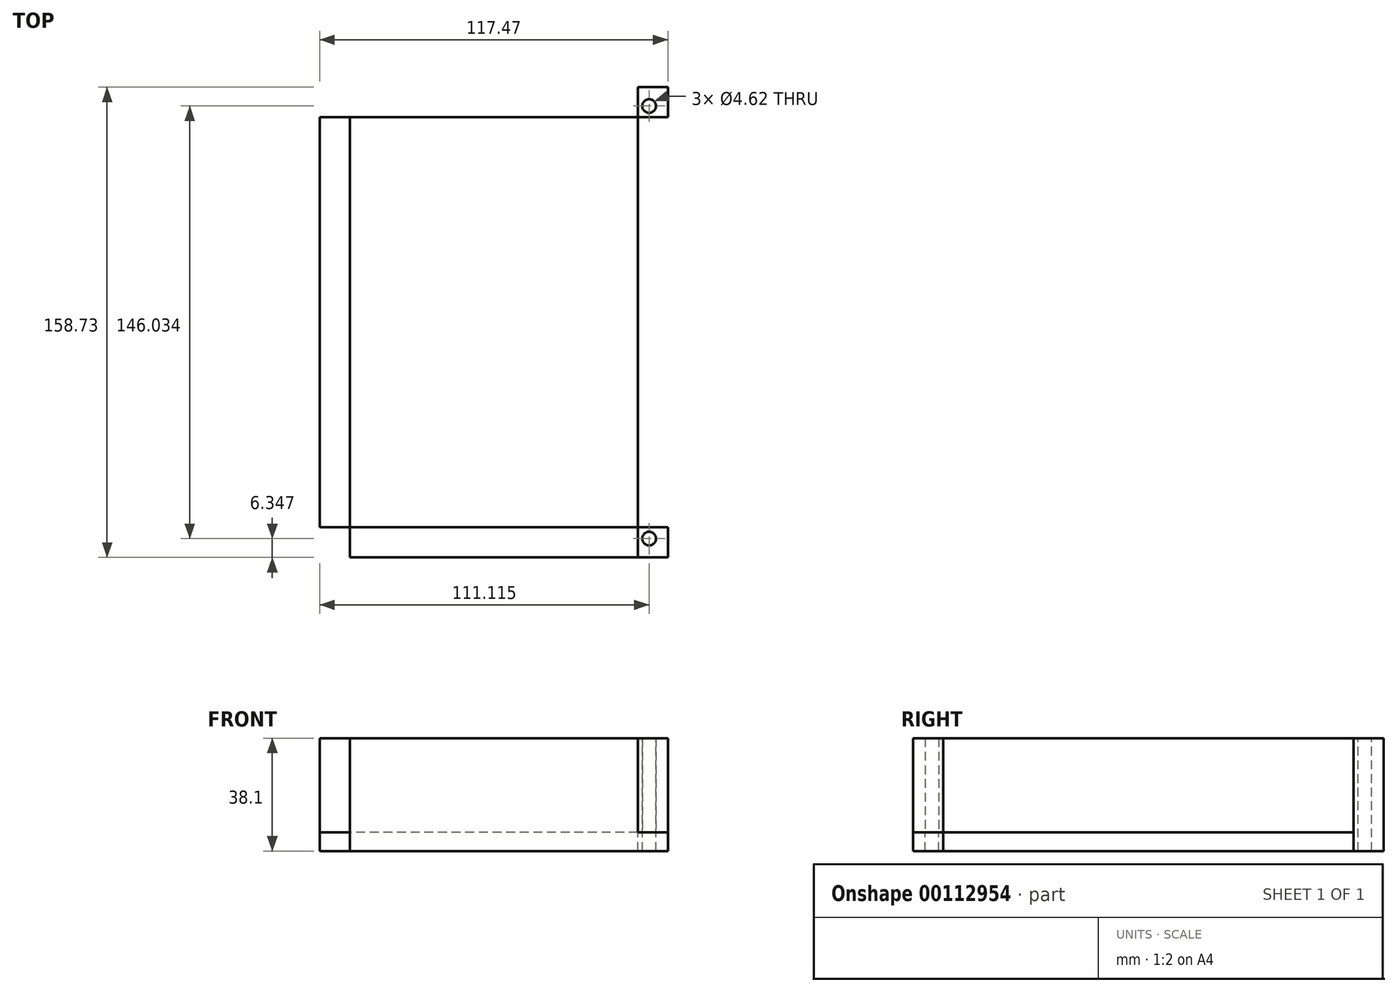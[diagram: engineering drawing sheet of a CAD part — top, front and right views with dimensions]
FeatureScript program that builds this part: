
annotation { "Feature Type Name" : "Feature", "Feature Type Description" : "" }
export const myFeature = defineFeature(function(context is Context, id is Id, definition is map)
    precondition{}
    {
        {
            var Q0;
            Q0=qCreatedBy(makeId("Top.planeOp"),FACE);
            var sketch = newSketch(context, id + "F0", { "sketchPlane" : qUnion([Q0])});
            skLineSegment(sketch, "E0", {"start": v(-95.22, 74.36) * mm, "end": v(-95.22, -84.37) * mm});
            skLineSegment(sketch, "E1", {"start": v(-95.22, 74.36) * mm, "end": v(22.25, 74.36) * mm});
            skLineSegment(sketch, "E2", {"start": v(22.25, 74.36) * mm, "end": v(22.25, -84.37) * mm});
            skLineSegment(sketch, "E3", {"start": v(22.25, -84.37) * mm, "end": v(-95.22, -84.37) * mm});
            skLineSegment(sketch, "E4", {"start": v(-95.22, 74.36) * mm, "end": v(-85.06, 74.36) * mm});
            skLineSegment(sketch, "E5", {"start": v(22.25, 74.36) * mm, "end": v(12.09, 74.36) * mm});
            skLineSegment(sketch, "E6", {"start": v(-95.22, 74.36) * mm, "end": v(-95.22, 61.66) * mm});
            skLineSegment(sketch, "E7", {"start": v(22.25, 74.36) * mm, "end": v(22.25, 64.2) * mm});
            skLineSegment(sketch, "E8", {"start": v(22.25, 64.2) * mm, "end": v(22.25, 74.36) * mm});
            skLineSegment(sketch, "E9", {"start": v(-95.22, -84.37) * mm, "end": v(-85.06, -84.37) * mm});
            skLineSegment(sketch, "E10.bottom", {"start": v(-95.22, -84.37) * mm, "end": v(-95.22, -84.37) * mm});
            skLineSegment(sketch, "E10.top", {"start": v(-95.22, -74.21) * mm, "end": v(-95.22, -74.21) * mm});
            skLineSegment(sketch, "E10.left", {"start": v(-95.22, -84.37) * mm, "end": v(-95.22, -74.21) * mm});
            skLineSegment(sketch, "E10.right", {"start": v(-95.22, -84.37) * mm, "end": v(-95.22, -74.21) * mm});
            skLineSegment(sketch, "E11.bottom", {"start": v(22.25, -84.37) * mm, "end": v(22.25, -84.37) * mm});
            skLineSegment(sketch, "E11.top", {"start": v(22.25, -74.21) * mm, "end": v(22.25, -74.21) * mm});
            skLineSegment(sketch, "E11.left", {"start": v(22.25, -84.37) * mm, "end": v(22.25, -74.21) * mm});
            skLineSegment(sketch, "E11.right", {"start": v(22.25, -84.37) * mm, "end": v(22.25, -74.21) * mm});
            skLineSegment(sketch, "E12.bottom", {"start": v(22.25, -84.37) * mm, "end": v(12.09, -84.37) * mm});
            skLineSegment(sketch, "E12.top", {"start": v(22.25, -84.37) * mm, "end": v(12.09, -84.37) * mm});
            skLineSegment(sketch, "E12.right", {"start": v(12.09, -84.37) * mm, "end": v(12.09, -84.37) * mm});
            skLineSegment(sketch, "E13", {"start": v(12.09, -84.37) * mm, "end": v(22.25, -84.37) * mm});
            skPoint(sketch, "E14.centerSnap0", {"position": v(-95.22, 68.01) * mm});
            skPoint(sketch, "E15.centerSnap0", {"position": v(22.25, 69.28) * mm});
            skPoint(sketch, "E16.centerSnap0", {"position": v(22.25, -79.3) * mm});
            skPoint(sketch, "E17.centerSnap1", {"position": v(-95.22, -79.3) * mm});
            skLineSegment(sketch, "E18", {"start": v(-85.06, -74.21) * mm, "end": v(-85.06, 61.66) * mm});
            skLineSegment(sketch, "E19", {"start": v(12.09, 61.66) * mm, "end": v(12.09, -74.21) * mm});
            skLineSegment(sketch, "E20", {"start": v(12.09, -74.21) * mm, "end": v(-85.06, -74.21) * mm});
            skLineSegment(sketch, "E21", {"start": v(-85.06, 74.36) * mm, "end": v(-85.06, 61.66) * mm});
            skLineSegment(sketch, "E22", {"start": v(12.09, 74.36) * mm, "end": v(12.09, 61.66) * mm});
            skLineSegment(sketch, "E23", {"start": v(12.09, -74.21) * mm, "end": v(22.25, -74.21) * mm});
            skLineSegment(sketch, "E24", {"start": v(12.09, -74.21) * mm, "end": v(12.09, -84.37) * mm});
            skLineSegment(sketch, "E25", {"start": v(-95.22, -74.21) * mm, "end": v(-85.06, -74.21) * mm});
            skLineSegment(sketch, "E26", {"start": v(-85.02, -87.14) * mm, "end": v(-85.06, -74.21) * mm});
            skLineSegment(sketch, "E27", {"start": v(-85.06, 61.66) * mm, "end": v(-85.06, 48.96) * mm});
            skLineSegment(sketch, "E28", {"start": v(-85.06, 48.96) * mm, "end": v(-85.06, 61.66) * mm});
            skLineSegment(sketch, "E29", {"start": v(12.09, 48.96) * mm, "end": v(12.09, 61.66) * mm});
            skLineSegment(sketch, "E30", {"start": v(-72.36, -74.21) * mm, "end": v(-85.06, -74.21) * mm});
            skLineSegment(sketch, "E31", {"start": v(-85.06, -74.21) * mm, "end": v(-85.06, -61.51) * mm});
            skLineSegment(sketch, "E32", {"start": v(-0.61, -74.21) * mm, "end": v(12.09, -74.21) * mm});
            skLineSegment(sketch, "E33", {"start": v(12.09, -61.51) * mm, "end": v(12.09, -74.21) * mm});
            skLineSegment(sketch, "E34", {"start": v(-95.22, -84.37) * mm, "end": v(-88.87, -84.37) * mm});
            skLineSegment(sketch, "E35", {"start": v(22.25, -84.37) * mm, "end": v(15.9, -84.37) * mm});
            skLineSegment(sketch, "E36", {"start": v(15.9, -84.37) * mm, "end": v(22.25, -84.37) * mm});
            skLineSegment(sketch, "E37", {"start": v(-95.22, 74.36) * mm, "end": v(-88.87, 74.36) * mm});
            skLineSegment(sketch, "E38", {"start": v(-88.87, 74.36) * mm, "end": v(-95.22, 74.36) * mm});
            skLineSegment(sketch, "E39", {"start": v(22.25, 74.36) * mm, "end": v(15.9, 74.36) * mm});
            skLineSegment(sketch, "E40", {"start": v(22.25, 64.2) * mm, "end": v(-95.22, 64.2) * mm});
            skLineSegment(sketch, "E41", {"start": v(22.25, 74.36) * mm, "end": v(22.25, 68.01) * mm});
            skCircle(sketch, "E42", {"center": v(15.9, 68.01) * mm, "radius": 2.31 * mm});
            skLineSegment(sketch, "E43", {"start": v(-95.22, 74.36) * mm, "end": v(-95.22, 68.01) * mm});
            skCircle(sketch, "E44", {"center": v(-88.87, 68.01) * mm, "radius": 2.31 * mm});
            skLineSegment(sketch, "E45", {"start": v(-95.22, -84.37) * mm, "end": v(-95.22, -78.02) * mm});
            skCircle(sketch, "E46", {"center": v(-88.87, -78.02) * mm, "radius": 2.31 * mm});
            skLineSegment(sketch, "E47", {"start": v(22.25, -84.37) * mm, "end": v(22.25, -78.02) * mm});
            skCircle(sketch, "E48", {"center": v(15.9, -78.02) * mm, "radius": 2.31 * mm});
            skSolve(sketch);
        }
        {
            var Q0;
            Q0=makeQuery(id+"F0.imprint","IMPRINT",FACE,{"disambiguationData":[TD([[makeQuery(id+"F0.imprint","IMPRINT",EDGE,{"derivedFrom":sQuery(id+"F0.wireOp",EDGE,"E32")}),1.0]])]});
            var Q1;
            Q1=makeQuery(id+"F0.imprint","IMPRINT",FACE,{"disambiguationData":[TD([[makeQuery(id+"F0.imprint","IMPRINT",EDGE,{"derivedFrom":sQuery(id+"F0.wireOp",EDGE,"cZfFtAw6-LTCG-etWa-Laot-MlDrLfI1tADb")}),1.0]])]});
            var Q2;
            Q2=makeQuery(id+"F0.imprint","IMPRINT",FACE,{"disambiguationData":[TD([[makeQuery(id+"F0.imprint","IMPRINT",EDGE,{"derivedFrom":sQuery(id+"F0.wireOp",EDGE,"E30")}),-1.0]])]});
            var Q3;
            Q3=makeQuery(id+"F0.imprint","IMPRINT",FACE,{"disambiguationData":[TD([[makeQuery(id+"F0.imprint","IMPRINT",EDGE,{"derivedFrom":sQuery(id+"F0.wireOp",EDGE,"E29")}),1.0]])]});
            var Q4;
            Q4=makeQuery(id+"F0.imprint","IMPRINT",FACE,{"disambiguationData":[TD([[makeQuery(id+"F0.imprint","IMPRINT",EDGE,{"derivedFrom":sQuery(id+"F0.wireOp",EDGE,"E11.right")}),1.0]])]});
            var Q5;
            Q5=makeQuery(id+"F0.imprint","IMPRINT",FACE,{"disambiguationData":[TD([[makeQuery(id+"F0.imprint","IMPRINT",EDGE,{"derivedFrom":sQuery(id+"F0.wireOp",EDGE,"E4")}),-1.0]])]});
            var Q6;
            {var subQ0=sQuery(id+"F0.wireOp",EDGE,"E9");Q6=makeQuery(id+"F0.imprint","IMPRINT",FACE,{"disambiguationData":[TD([[makeQuery(id+"F0.imprint","IMPRINT",EDGE,{"derivedFrom":subQ0}),1.0]])]});}
            var Q7;
            Q7=makeQuery(id+"F0.imprint","IMPRINT",FACE,{"disambiguationData":[TD([[makeQuery(id+"F0.imprint","IMPRINT",EDGE,{"derivedFrom":sQuery(id+"F0.wireOp",EDGE,"E18")}),-1.0]])]});
            var Q8;
            Q8=makeQuery(id+"F0.imprint","IMPRINT",FACE,{"disambiguationData":[TD([[makeQuery(id+"F0.imprint","IMPRINT",EDGE,{"derivedFrom":sQuery(id+"F0.wireOp",EDGE,"E2")}),-1.0]])]});
            var Q9;
            Q9=makeQuery(id+"F0.imprint","IMPRINT",FACE,{"disambiguationData":[TD([[makeQuery(id+"F0.imprint","IMPRINT",EDGE,{"derivedFrom":sQuery(id+"F0.wireOp",EDGE,"E20")}),1.0]])]});
            var Q10;
            Q10=makeQuery(id+"F0.imprint","IMPRINT",FACE,{"disambiguationData":[TD([[makeQuery(id+"F0.imprint","IMPRINT",EDGE,{"derivedFrom":sQuery(id+"F0.wireOp",EDGE,"E1")}),-1.0]])]});
            var Q11;
            Q11=makeQuery(id+"F0.imprint","IMPRINT",FACE,{"disambiguationData":[TD([[makeQuery(id+"F0.imprint","IMPRINT",EDGE,{"derivedFrom":sQuery(id+"F0.wireOp",EDGE,"E0")}),1.0]])]});
            var Q12;
            Q12=makeQuery(id+"F0.imprint","IMPRINT",FACE,{"disambiguationData":[TD([[makeQuery(id+"F0.imprint","IMPRINT",EDGE,{"derivedFrom":sQuery(id+"F0.wireOp",EDGE,"E5")}),1.0]])]});
            extrude(context, id + "F1", {"entities" : qUnion([Q0, Q1, Q2, Q3, Q4, Q5, Q6, Q7, Q8, Q9, Q10, Q11, Q12]), "oppositeDirection" : true, "depth" : 6.35 * mm});
        }
        {
            var Q0;
            Q0=makeQuery(id+"F0.imprint","IMPRINT",FACE,{"disambiguationData":[TD([[makeQuery(id+"F0.imprint","IMPRINT",EDGE,{"derivedFrom":sQuery(id+"F0.wireOp",EDGE,"E1")}),-1.0]])]});
            extrude(context, id + "F2", {"entities" : qUnion([Q0]), "operationType" : NewBodyOperationType.ADD, "depth" : 31.75 * mm});
        }
        {
            var Q0;
            Q0=makeQuery(id+"F0.imprint","IMPRINT",FACE,{"disambiguationData":[TD([[makeQuery(id+"F0.imprint","IMPRINT",EDGE,{"derivedFrom":sQuery(id+"F0.wireOp",EDGE,"E20")}),1.0]])]});
            extrude(context, id + "F3", {"entities" : qUnion([Q0]), "operationType" : NewBodyOperationType.ADD, "depth" : 31.75 * mm});
        }
        {
            var Q0;
            Q0=makeQuery(id+"F0.imprint","IMPRINT",FACE,{"disambiguationData":[TD([[makeQuery(id+"F0.imprint","IMPRINT",EDGE,{"derivedFrom":sQuery(id+"F0.wireOp",EDGE,"E2")}),-1.0]])]});
            extrude(context, id + "F4", {"entities" : qUnion([Q0]), "depth" : 31.75 * mm});
        }
        {
            var Q0;
            Q0=makeQuery(id+"F0.imprint","IMPRINT",FACE,{"disambiguationData":[TD([[makeQuery(id+"F0.imprint","IMPRINT",EDGE,{"derivedFrom":sQuery(id+"F0.wireOp",EDGE,"E0")}),1.0]])]});
            extrude(context, id + "F5", {"entities" : qUnion([Q0]), "depth" : 31.75 * mm});
        }
        {
            var Q0;
            Q0=makeQuery(id+"F4.opExtrude","SWEPT_FACE",FACE,{"disambiguationData":[OSD([sQuery(id+"F0.wireOp",EDGE,"E2")])]});
            var sketch = newSketch(context, id + "F6", { "sketchPlane" : qUnion([Q0])});
            skLineSegment(sketch, "E49", {"start": v(-74.21, 17.33) * mm, "end": v(-39.92, 17.33) * mm});
            skLineSegment(sketch, "E50", {"start": v(-31.99, 31.75) * mm, "end": v(-31.99, 19.05) * mm});
            skLineSegment(sketch, "E51.bottom", {"start": v(-39.92, 19.05) * mm, "end": v(-19.6, 19.05) * mm});
            skLineSegment(sketch, "E51.top", {"start": v(-39.92, 2.8) * mm, "end": v(-19.6, 2.8) * mm});
            skLineSegment(sketch, "E51.left", {"start": v(-39.92, 19.05) * mm, "end": v(-39.92, 2.8) * mm});
            skLineSegment(sketch, "E51.right", {"start": v(-19.6, 19.05) * mm, "end": v(-19.6, 2.8) * mm});
            skSolve(sketch);
        }
        {
            var Q0;
            {var subQ4=sQuery(id+"F6.wireOp",EDGE,"E51.top");Q0=makeQuery(id+"F6.imprint","IMPRINT",FACE,{"disambiguationData":[TD([[makeQuery(id+"F6.imprint","IMPRINT",EDGE,{"derivedFrom":subQ4}),1.0]])]});}
            extrude(context, id + "F7", {"entities" : qUnion([Q0]), "operationType" : NewBodyOperationType.REMOVE, "oppositeDirection" : true, "depth" : 10.16 * mm});
        }
    });
